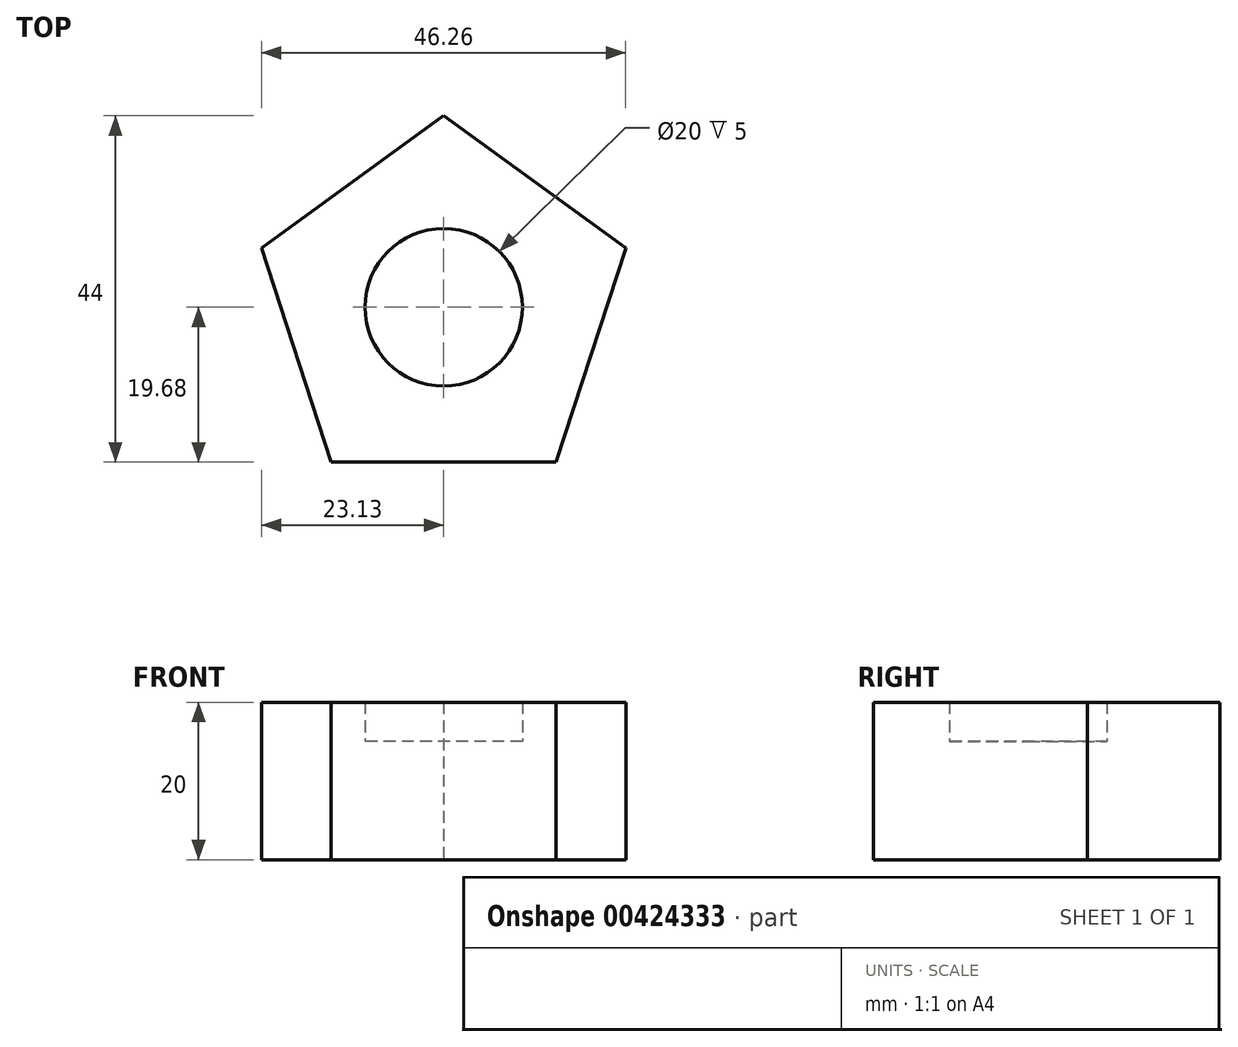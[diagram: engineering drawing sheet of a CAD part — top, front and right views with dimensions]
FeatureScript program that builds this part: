
annotation { "Feature Type Name" : "Feature", "Feature Type Description" : "" }
export const myFeature = defineFeature(function(context is Context, id is Id, definition is map)
    precondition{}
    {
        {
            var Q0;
            Q0=qCreatedBy(makeId("Top.planeOp"),FACE);
            var sketch = newSketch(context, id + "F0", { "sketchPlane" : qUnion([Q0])});
            skCircle(sketch, "E0.cCircle", {"center": v(0, 0) * mm, "radius": 24.32 * mm, "construction": true});
            skLineSegment(sketch, "E0.0", {"start": v(0, 24.32) * mm, "end": v(23.13, 7.52) * mm});
            skLineSegment(sketch, "E0.1", {"start": v(23.13, 7.52) * mm, "end": v(14.3, -19.68) * mm});
            skLineSegment(sketch, "E0.2", {"start": v(14.3, -19.68) * mm, "end": v(-14.3, -19.68) * mm});
            skLineSegment(sketch, "E0.3", {"start": v(-14.3, -19.68) * mm, "end": v(-23.13, 7.52) * mm});
            skLineSegment(sketch, "E0.4", {"start": v(-23.13, 7.52) * mm, "end": v(0, 24.32) * mm});
            skLineSegment(sketch, "E1", {"start": v(0, 24.32) * mm, "end": v(0, -19.68) * mm});
            skSolve(sketch);
        }
        {
            var Q0;
            {var subQ0=sQuery(id+"F0.wireOp",EDGE,"E0.3");Q0=makeQuery(id+"F0.imprint","IMPRINT",FACE,{"disambiguationData":[TD([[makeQuery(id+"F0.imprint","IMPRINT",EDGE,{"derivedFrom":subQ0}),-1.0]])]});}
            var Q1;
            Q1=makeQuery(id+"F0.imprint","IMPRINT",FACE,{"disambiguationData":[TD([[makeQuery(id+"F0.imprint","IMPRINT",EDGE,{"derivedFrom":sQuery(id+"F0.wireOp",EDGE,"E0.0")}),-1.0]])]});
            extrude(context, id + "F1", {"entities" : qUnion([Q0, Q1]), "depth" : 15 * mm, "offsetDistance" : 25 * mm});
        }
        {
            var Q0;
            Q0=makeQuery(id+"F1.opExtrude","CAP_FACE",FACE,{"disambiguationData":[OSD([sQuery(id+"F0.wireOp",EDGE,"E0.0"),sQuery(id+"F0.wireOp",EDGE,"E0.1"),sQuery(id+"F0.wireOp",EDGE,"E0.2"),sQuery(id+"F0.wireOp",EDGE,"E0.3"),sQuery(id+"F0.wireOp",EDGE,"E0.4")])],"isStart":false});
            var sketch = newSketch(context, id + "F2", { "sketchPlane" : qUnion([Q0])});
            skCircle(sketch, "E2", {"center": v(0, 0) * mm, "radius": 10 * mm});
            skLineSegment(sketch, "E3", {"start": v(0, 0) * mm, "end": v(10, 0) * mm});
            skSolve(sketch);
        }
        {
            var Q0;
            Q0=makeQuery(id+"F2.imprint","IMPRINT",FACE,{"disambiguationData":[TD([[makeQuery(id+"F2.imprint","IMPRINT",EDGE,{"derivedFrom":sQuery(id+"F2.wireOp",EDGE,"E2")}),-1.0]])]});
            extrude(context, id + "F3", {"entities" : qUnion([Q0]), "operationType" : NewBodyOperationType.ADD, "depth" : 5 * mm, "offsetDistance" : 25 * mm});
        }
    });
